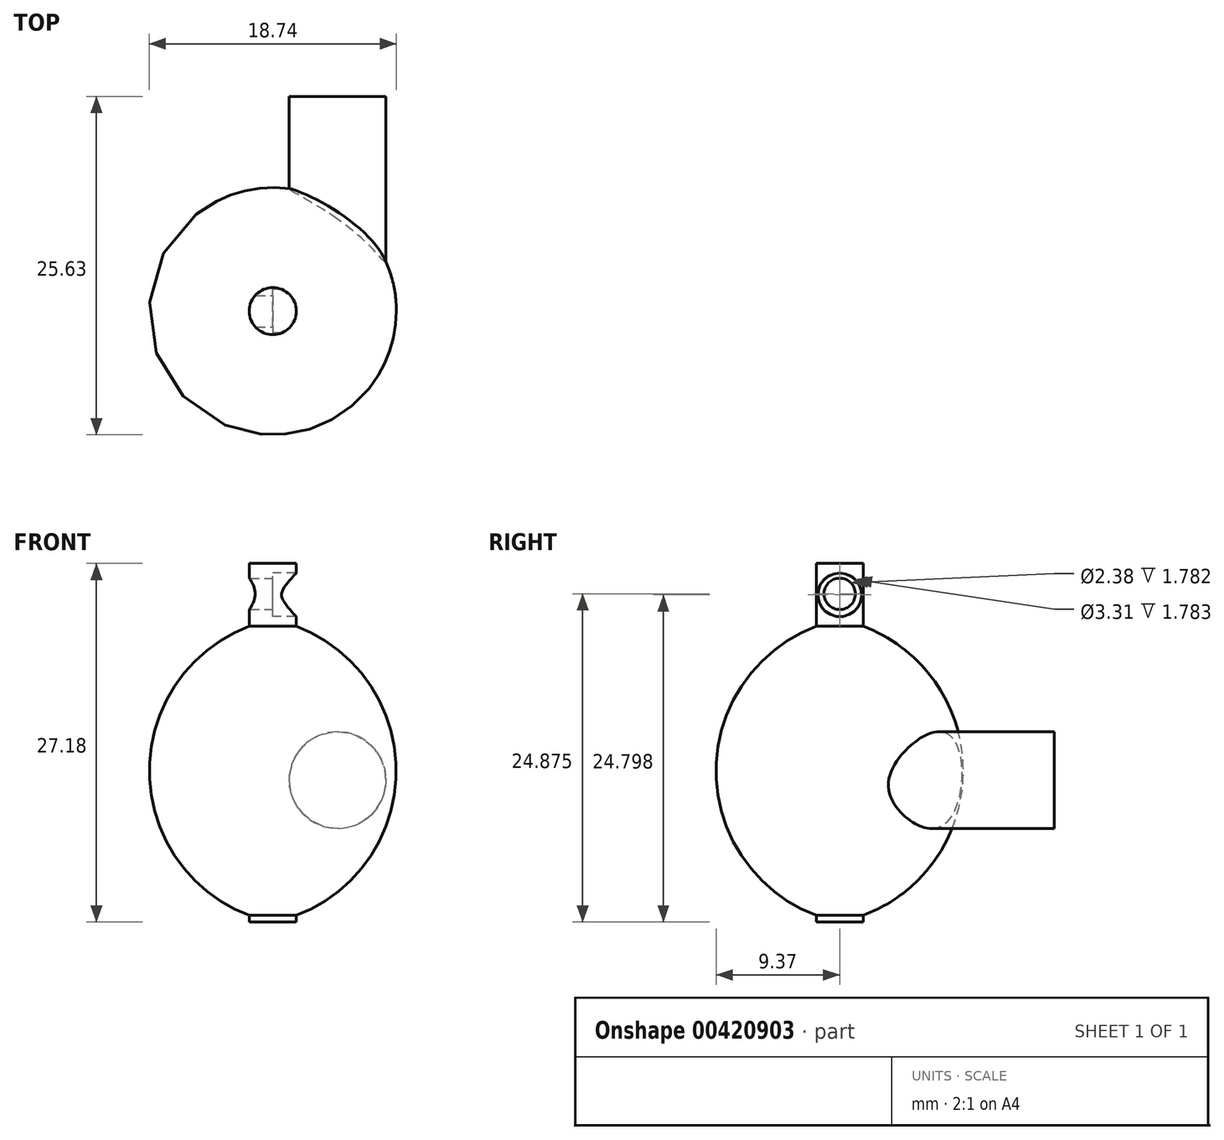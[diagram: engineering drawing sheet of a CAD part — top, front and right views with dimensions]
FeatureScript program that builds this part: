
annotation { "Feature Type Name" : "Feature", "Feature Type Description" : "" }
export const myFeature = defineFeature(function(context is Context, id is Id, definition is map)
    precondition{}
    {
        {
            var Q0;
            Q0=qCreatedBy(makeId("Front.planeOp"),FACE);
            var sketch = newSketch(context, id + "F0", { "sketchPlane" : qUnion([Q0])});
            skLineSegment(sketch, "E0", {"start": v(0, 0) * mm, "end": v(0, 22.93) * mm});
            skArc(sketch, "E1", {"start": v(0, 0) * mm, "mid": v(9.37, 11.46) * mm, "end": v(0, 22.93) * mm});
            skSolve(sketch);
        }
        {
            var Q0;
            Q0=makeQuery(id+"F0.imprint","IMPRINT",FACE,{"disambiguationData":[TD([[makeQuery(id+"F0.imprint","IMPRINT",EDGE,{"derivedFrom":sQuery(id+"F0.wireOp",EDGE,"E0")}),-1.0]])]});
            var Q1;
            Q1=sQuery(id+"F0.wireOp",EDGE,"E0");
            revolve(context, id + "F1", {"entities" : qUnion([Q0]), "axis" : qUnion([Q1]), "revolveType" : RevolveType.FULL});
        }
        {
            var Q0;
            Q0=qCreatedBy(makeId("Front.planeOp"),FACE);
            var sketch = newSketch(context, id + "F2", { "sketchPlane" : qUnion([Q0])});
            skCircle(sketch, "E2", {"center": v(-3.5, 10.06) * mm, "radius": 4.47 * mm});
            skSolve(sketch);
        }
        {
            var Q0;
            Q0=sQuery(id+"F2.wireOp",EDGE,"E2");
            extrude(context, id + "F3", {"bodyType" : ToolBodyType.SURFACE, "surfaceEntities" : qUnion([Q0]), "depth" : 16.26 * mm});
        }
        {
            var Q0;
            Q0=qCreatedBy(makeId("Front.planeOp"),FACE);
            var sketch = newSketch(context, id + "F4", { "sketchPlane" : qUnion([Q0])});
            skCircle(sketch, "E3", {"center": v(4.91, 10.76) * mm, "radius": 3.66 * mm});
            skSolve(sketch);
        }
        {
            var Q0;
            Q0 = qSketchRegion(id + "F4", true);
            extrude(context, id + "F5", {"entities" : qUnion([Q0]), "operationType" : NewBodyOperationType.ADD, "oppositeDirection" : true, "depth" : 16.26 * mm});
        }
        {
            var Q0;
            Q0=qCreatedBy(makeId("Top.planeOp"),FACE);
            var sketch = newSketch(context, id + "F6", { "sketchPlane" : qUnion([Q0])});
            skCircle(sketch, "E4", {"center": v(0, 0) * mm, "radius": 1.78 * mm});
            skSolve(sketch);
        }
        {
            var Q0;
            Q0 = qSketchRegion(id + "F6", true);
            extrude(context, id + "F7", {"entities" : qUnion([Q0]), "operationType" : NewBodyOperationType.ADD, "depth" : 27.18 * mm});
        }
        {
            var Q0;
            Q0=qCreatedBy(makeId("Right.planeOp"),FACE);
            var sketch = newSketch(context, id + "F8", { "sketchPlane" : qUnion([Q0])});
            skCircle(sketch, "E5", {"center": v(0, 24.88) * mm, "radius": 1.19 * mm});
            skSolve(sketch);
        }
        {
            var Q0;
            Q0 = qSketchRegion(id + "F8", true);
            extrude(context, id + "F9", {"entities" : qUnion([Q0]), "operationType" : NewBodyOperationType.REMOVE, "oppositeDirection" : true, "depth" : 72.14 * mm});
        }
        {
            var Q0;
            Q0=qCreatedBy(makeId("Right.planeOp"),FACE);
            var sketch = newSketch(context, id + "F10", { "sketchPlane" : qUnion([Q0])});
            skCircle(sketch, "E6", {"center": v(0, 24.8) * mm, "radius": 1.65 * mm});
            skSolve(sketch);
        }
        {
            var Q0;
            Q0 = qSketchRegion(id + "F10", true);
            extrude(context, id + "F11", {"entities" : qUnion([Q0]), "operationType" : NewBodyOperationType.REMOVE, "depth" : 132.6 * mm});
        }
    });
